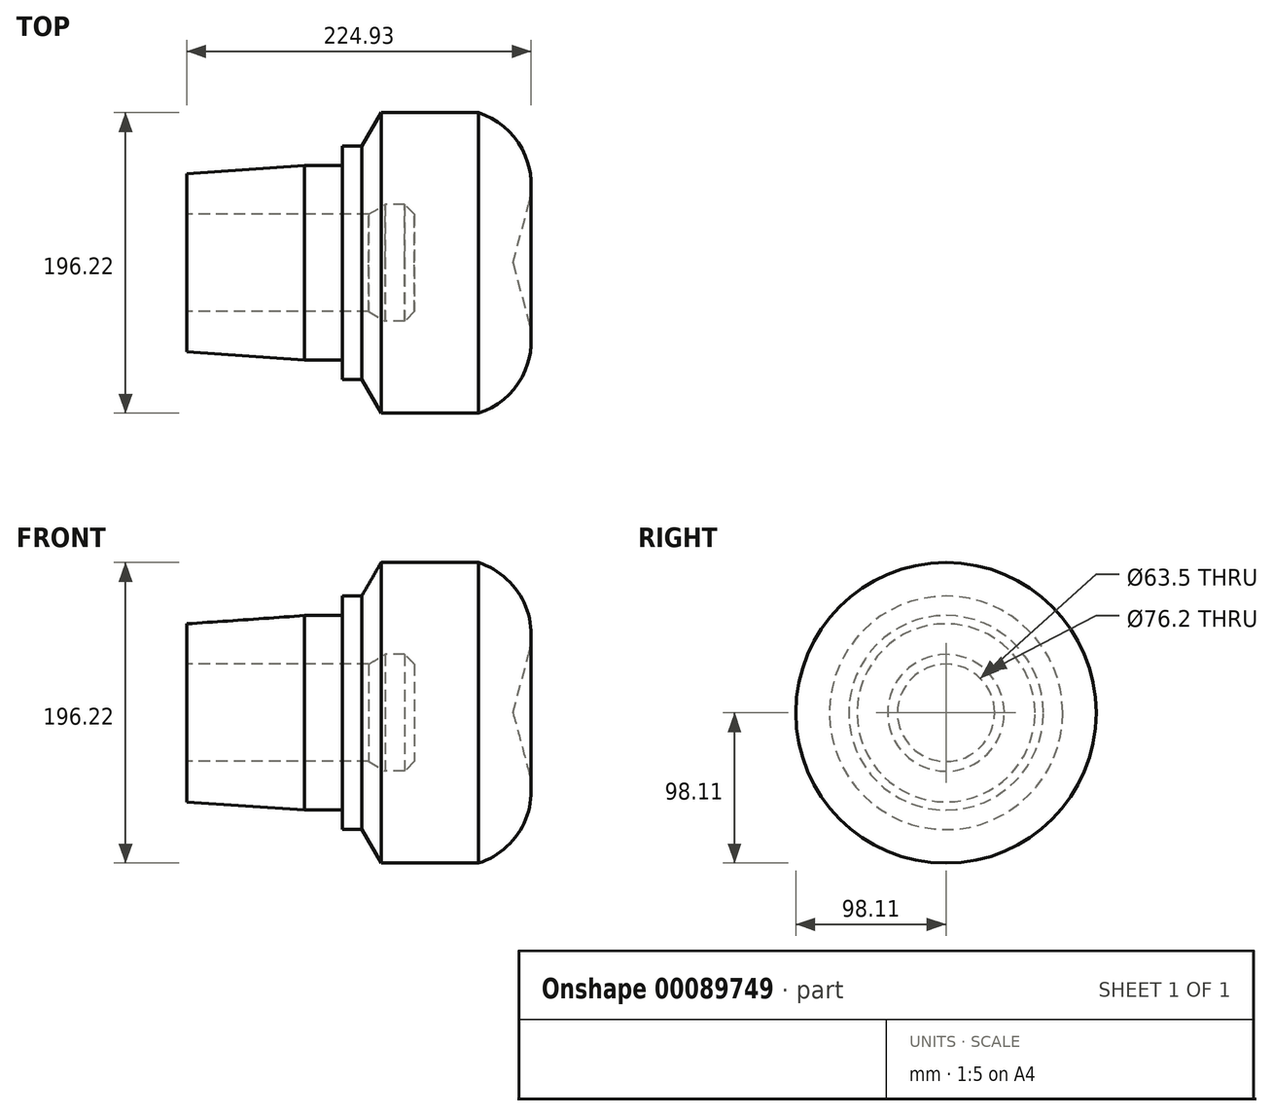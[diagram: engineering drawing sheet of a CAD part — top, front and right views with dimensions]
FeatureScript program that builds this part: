
annotation { "Feature Type Name" : "Feature", "Feature Type Description" : "" }
export const myFeature = defineFeature(function(context is Context, id is Id, definition is map)
    precondition{}
    {
        {
            var Q0;
            Q0=qCreatedBy(makeId("Front.planeOp"),FACE);
            var sketch = newSketch(context, id + "F0", { "sketchPlane" : qUnion([Q0])});
            skLineSegment(sketch, "E0", {"start": v(-114.3, 31.75) * mm, "end": v(-114.3, 58.11) * mm});
            skLineSegment(sketch, "E1", {"start": v(-12.7, 76.2) * mm, "end": v(0, 76.2) * mm});
            skLineSegment(sketch, "E2", {"start": v(0, 76.2) * mm, "end": v(12.65, 98.1) * mm});
            skLineSegment(sketch, "E3", {"start": v(12.65, 98.1) * mm, "end": v(76.15, 98.1) * mm});
            skArc(sketch, "E4", {"start": v(108.94, 38.1) * mm, "mid": v(104.56, 74.67) * mm, "end": v(76.15, 98.1) * mm});
            skLineSegment(sketch, "E5", {"start": v(108.94, 38.1) * mm, "end": v(98.73, 0) * mm});
            skLineSegment(sketch, "E6", {"start": v(98.73, 0) * mm, "end": v(34.43, 0) * mm});
            skLineSegment(sketch, "E7", {"start": v(28.08, 38.1) * mm, "end": v(15.38, 38.1) * mm});
            skLineSegment(sketch, "E8", {"start": v(15.38, 38.1) * mm, "end": v(4.38, 31.75) * mm});
            skLineSegment(sketch, "E9", {"start": v(4.38, 31.75) * mm, "end": v(-114.3, 31.75) * mm});
            skLineSegment(sketch, "E10", {"start": v(-12.7, 76.2) * mm, "end": v(-12.7, 63.5) * mm});
            skLineSegment(sketch, "E11", {"start": v(-12.7, 63.5) * mm, "end": v(-37.29, 63.5) * mm});
            skLineSegment(sketch, "E12", {"start": v(-37.29, 63.5) * mm, "end": v(-114.3, 58.11) * mm});
            skLineSegment(sketch, "E13", {"start": v(-132.54, 0) * mm, "end": v(234.4, 0) * mm, "construction": true});
            skLineSegment(sketch, "E14", {"start": v(110.63, 98.1) * mm, "end": v(110.63, 0) * mm, "construction": true});
            skLineSegment(sketch, "E15", {"start": v(34.43, 0) * mm, "end": v(34.43, 31.75) * mm});
            skLineSegment(sketch, "E16", {"start": v(34.43, 31.75) * mm, "end": v(28.08, 38.1) * mm});
            skSolve(sketch);
        }
        {
            var Q0;
            Q0 = qSketchRegion(id + "F0", true);
            var Q1;
            Q1=sQuery(id+"F0.wireOp",EDGE,"E13");
            revolve(context, id + "F1", {"entities" : qUnion([Q0]), "axis" : qUnion([Q1]), "revolveType" : RevolveType.FULL});
        }
    });
